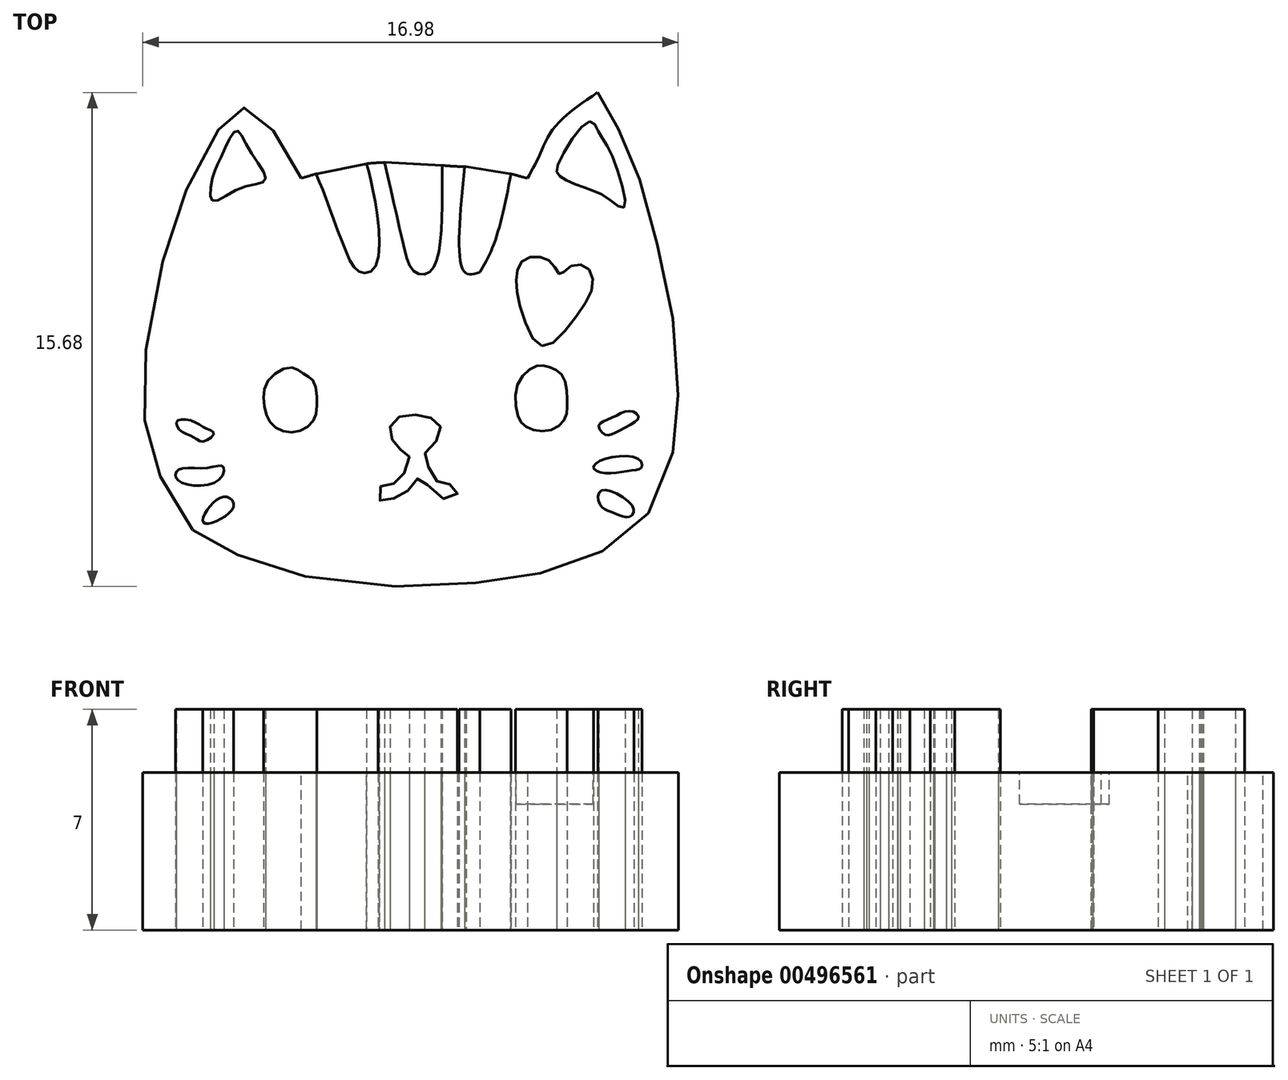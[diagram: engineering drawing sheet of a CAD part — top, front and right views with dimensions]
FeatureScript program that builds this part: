
annotation { "Feature Type Name" : "Feature", "Feature Type Description" : "" }
export const myFeature = defineFeature(function(context is Context, id is Id, definition is map)
    precondition{}
    {
        {
            var Q0;
            Q0=qCreatedBy(makeId("Top.planeOp"),FACE);
            var sketch = newSketch(context, id + "F0", { "sketchPlane" : qUnion([Q0])});
            skFitSpline(sketch, "E0", {"points": [v(16.94, 17.8) * mm, v(17.2, 17.42) * mm, v(17.74, 16.37) * mm, v(18.24, 15.15) * mm, v(18.74, 13.3) * mm, v(19.29, 10.91) * mm, v(19.5, 8.23) * mm, v(19.42, 6.84) * mm, v(18.87, 4.95) * mm, v(17.86, 3.74) * mm, v(16.35, 2.9) * mm, v(14.46, 2.4) * mm, v(12.5, 2.18) * mm, v(9.18, 2.18) * mm, v(6.15, 2.86) * mm, v(4.94, 3.4) * mm, v(3.93, 4.07) * mm, v(3.05, 5.67) * mm, v(2.63, 7.1) * mm, v(2.55, 8.94) * mm, v(3.13, 12.38) * mm, v(3.93, 14.77) * mm, v(4.9, 16.58) * mm, v(5.4, 17.46) * mm, v(5.86, 17.2) * mm, v(6.24, 16.96) * mm, v(6.87, 16.33) * mm, v(7.54, 15.07) * mm], "startDerivative": vector(11.95, -16.58) * mm, "endDerivative": vector(17.95, -39.41) * mm});
            skFitSpline(sketch, "E1", {"points": [v(7.54, 15.07) * mm, v(9, 15.44) * mm, v(10.77, 15.57) * mm, v(12.45, 15.44) * mm, v(13.29, 15.4) * mm, v(14.72, 15.07) * mm], "startDerivative": vector(6.98, 2.07) * mm, "endDerivative": vector(7.67, -2.1) * mm});
            skFitSpline(sketch, "E2", {"points": [v(14.72, 15.07) * mm, v(15.1, 15.78) * mm, v(15.55, 16.66) * mm, v(16.94, 17.8) * mm], "startDerivative": vector(1.42, 2.49) * mm, "endDerivative": vector(3.9, 2.68) * mm});
            skFitSpline(sketch, "E3", {"points": [v(15, 9.1) * mm, v(15.43, 9.07) * mm, v(15.85, 8.77) * mm, v(15.97, 8.02) * mm, v(15.93, 7.51) * mm, v(15.51, 7.1) * mm, v(14.76, 7.14) * mm, v(14.42, 7.51) * mm, v(14.42, 8.56) * mm, v(15, 9.1) * mm]});
            skFitSpline(sketch, "E4", {"points": [v(7.25, 9.07) * mm, v(7.62, 8.86) * mm, v(7.92, 8.65) * mm, v(8.04, 7.93) * mm, v(7.88, 7.3) * mm, v(7.25, 7) * mm, v(6.62, 7.26) * mm, v(6.36, 7.9) * mm, v(6.5, 8.65) * mm, v(7.25, 9.07) * mm]});
            skFitSpline(sketch, "E5", {"points": [v(4.73, 14.35) * mm, v(4.73, 15.07) * mm, v(5.02, 15.78) * mm, v(5.48, 16.58) * mm, v(5.86, 16.03) * mm, v(6.4, 15.02) * mm, v(5.65, 14.77) * mm, v(4.73, 14.35) * mm]});
            skFitSpline(sketch, "E6", {"points": [v(16.69, 16.87) * mm, v(16.98, 16.54) * mm, v(17.4, 15.78) * mm, v(17.78, 14.14) * mm, v(17.2, 14.48) * mm, v(16.4, 14.82) * mm, v(15.72, 15.15) * mm, v(15.68, 15.49) * mm, v(16.69, 16.87) * mm]});
            skFitSpline(sketch, "E7", {"points": [v(13.2, 12.09) * mm, v(13.67, 13.01) * mm, v(14.2, 15.2) * mm], "startDerivative": vector(1.2, 2) * mm, "endDerivative": vector(0.82, 4.1) * mm});
            skFitSpline(sketch, "E8", {"points": [v(14.2, 15.2) * mm, v(13.29, 15.4) * mm, v(12.45, 15.44) * mm], "startDerivative": vector(-1.79, 0.45) * mm, "endDerivative": vector(-1.7, 0.02) * mm});
            skFitSpline(sketch, "E9", {"points": [v(13.2, 12.09) * mm, v(12.73, 12.09) * mm, v(12.73, 15.44) * mm], "startDerivative": vector(-1.98, -0.63) * mm, "endDerivative": vector(0.63, 6.3) * mm});
            skFitSpline(sketch, "E10", {"points": [v(12.73, 15.44) * mm, v(14.2, 15.2) * mm], "startDerivative": vector(1.47, -0.23) * mm, "endDerivative": vector(1.47, -0.23) * mm});
            skFitSpline(sketch, "E11", {"points": [v(10.2, 15.57) * mm, v(10.77, 13.01) * mm, v(11.15, 12.09) * mm, v(11.6, 12.09) * mm, v(11.95, 13.01) * mm, v(12.01, 15.48) * mm], "startDerivative": vector(2.28, -10.08) * mm, "endDerivative": vector(-0.07, 9.99) * mm});
            skFitSpline(sketch, "E12", {"points": [v(12.01, 15.48) * mm, v(10.2, 15.57) * mm], "startDerivative": vector(-1.82, 0.1) * mm, "endDerivative": vector(-1.82, 0.1) * mm});
            skFitSpline(sketch, "E13", {"points": [v(8.02, 15.2) * mm, v(8.42, 14.19) * mm, v(9, 12.63) * mm, v(9.43, 12.09) * mm, v(9.89, 12.26) * mm, v(9.89, 14.31) * mm, v(9.62, 15.53) * mm], "startDerivative": vector(2.34, -5.71) * mm, "endDerivative": vector(-1.55, 5.88) * mm});
            skFitSpline(sketch, "E14", {"points": [v(9.62, 15.53) * mm, v(8.02, 15.2) * mm], "startDerivative": vector(-1.6, -0.32) * mm, "endDerivative": vector(-1.6, -0.32) * mm});
            skFitSpline(sketch, "E15", {"points": [v(10.06, 5.29) * mm, v(10.48, 5.37) * mm, v(10.85, 5.8) * mm, v(10.94, 6.34) * mm, v(10.6, 6.5) * mm, v(10.4, 6.88) * mm, v(10.4, 7.26) * mm, v(10.81, 7.56) * mm, v(11.44, 7.51) * mm, v(11.86, 7.35) * mm, v(11.95, 6.88) * mm, v(11.48, 6.38) * mm, v(11.57, 5.92) * mm, v(11.9, 5.41) * mm, v(12.32, 5.33) * mm, v(12.5, 5.04) * mm, v(11.9, 4.95) * mm, v(11.32, 5.58) * mm, v(11.02, 5.25) * mm, v(10.56, 4.95) * mm, v(10.06, 4.83) * mm, v(10.06, 5.29) * mm]});
            skFitSpline(sketch, "E16", {"points": [v(17.4, 7.47) * mm, v(17.99, 7.68) * mm, v(18.24, 7.47) * mm, v(17.61, 7.05) * mm, v(17.2, 6.93) * mm, v(16.98, 7.22) * mm, v(17.4, 7.47) * mm]});
            skFitSpline(sketch, "E17", {"points": [v(17.2, 6.17) * mm, v(18.28, 6.13) * mm, v(18.32, 5.88) * mm, v(17.99, 5.8) * mm, v(17.2, 5.7) * mm, v(16.81, 5.88) * mm, v(17.2, 6.17) * mm]});
            skFitSpline(sketch, "E18", {"points": [v(17.07, 5.16) * mm, v(18.07, 4.62) * mm, v(17.95, 4.32) * mm, v(17.44, 4.45) * mm, v(17.02, 4.7) * mm, v(17.07, 5.16) * mm]});
            skFitSpline(sketch, "E19", {"points": [v(4.43, 6.72) * mm, v(4.14, 6.84) * mm, v(3.72, 7.05) * mm, v(3.6, 7.35) * mm, v(4.01, 7.39) * mm, v(4.52, 7.14) * mm, v(4.77, 6.97) * mm, v(4.43, 6.72) * mm]});
            skFitSpline(sketch, "E20", {"points": [v(4.56, 5.88) * mm, v(3.68, 5.83) * mm, v(3.55, 5.62) * mm, v(3.85, 5.37) * mm, v(4.94, 5.5) * mm, v(5.06, 5.92) * mm, v(4.56, 5.88) * mm]});
            skFitSpline(sketch, "E21", {"points": [v(4.64, 4.66) * mm, v(5.19, 4.95) * mm, v(5.4, 4.66) * mm, v(4.77, 4.16) * mm, v(4.43, 4.16) * mm, v(4.64, 4.66) * mm]});
            skFitSpline(sketch, "E22", {"points": [v(15.18, 9.74) * mm, v(16.23, 10.64) * mm, v(16.8, 11.74) * mm, v(16.54, 12.28) * mm, v(16.02, 12.24) * mm, v(15.76, 12.02) * mm, v(15.54, 12.31) * mm, v(15.15, 12.56) * mm, v(14.59, 12.47) * mm, v(14.37, 11.96) * mm, v(14.5, 11) * mm, v(15.18, 9.74) * mm]});
            skSolve(sketch);
        }
        {
            var Q0;
            {var subQ0=sQuery(id+"F0.wireOp",EDGE,"E13");var subQ1=sQuery(id+"F0.wireOp",EDGE,"E1");var subQ2=makeQuery(id+"F0.imprint","INTERSECT",VERTEX,{"derivedFrom":[subQ1,subQ0]});Q0=makeQuery(id+"F0.imprint","IMPRINT",FACE,{"disambiguationData":[TD([[makeQuery(id+"F0.imprint","IMPRINT",EDGE,{"disambiguationData":[TD([[subQ2,-1.0]])],"derivedFrom":subQ1}),-1.0]])]});}
            var Q1;
            Q1=makeQuery(id+"F0.imprint","IMPRINT",FACE,{"disambiguationData":[TD([[makeQuery(id+"F0.imprint","IMPRINT",EDGE,{"derivedFrom":sQuery(id+"F0.wireOp",EDGE,"E11")}),1.0]])]});
            var Q2;
            {var subQ0=sQuery(id+"F0.wireOp",EDGE,"E9");var subQ3=sQuery(id+"F0.wireOp",EDGE,"E1");var subQ4=makeQuery(id+"F0.imprint","INTERSECT",VERTEX,{"derivedFrom":[subQ3,subQ0]});Q2=makeQuery(id+"F0.imprint","IMPRINT",FACE,{"disambiguationData":[TD([[makeQuery(id+"F0.imprint","IMPRINT",EDGE,{"disambiguationData":[TD([[subQ4,-1.0]])],"derivedFrom":subQ3}),-1.0]])]});}
            var Q3;
            Q3=makeQuery(id+"F0.imprint","IMPRINT",FACE,{"disambiguationData":[TD([[makeQuery(id+"F0.imprint","IMPRINT",EDGE,{"derivedFrom":sQuery(id+"F0.wireOp",EDGE,"E6")}),-1.0]])]});
            var Q4;
            Q4=makeQuery(id+"F0.imprint","IMPRINT",FACE,{"disambiguationData":[TD([[makeQuery(id+"F0.imprint","IMPRINT",EDGE,{"derivedFrom":sQuery(id+"F0.wireOp",EDGE,"E5")}),-1.0]])]});
            var Q5;
            Q5=makeQuery(id+"F0.imprint","IMPRINT",FACE,{"disambiguationData":[TD([[makeQuery(id+"F0.imprint","IMPRINT",EDGE,{"derivedFrom":sQuery(id+"F0.wireOp",EDGE,"E4")}),-1.0]])]});
            var Q6;
            Q6=makeQuery(id+"F0.imprint","IMPRINT",FACE,{"disambiguationData":[TD([[makeQuery(id+"F0.imprint","IMPRINT",EDGE,{"derivedFrom":sQuery(id+"F0.wireOp",EDGE,"E21")}),-1.0]])]});
            var Q7;
            Q7=makeQuery(id+"F0.imprint","IMPRINT",FACE,{"disambiguationData":[TD([[makeQuery(id+"F0.imprint","IMPRINT",EDGE,{"derivedFrom":sQuery(id+"F0.wireOp",EDGE,"E20")}),1.0]])]});
            var Q8;
            Q8=makeQuery(id+"F0.imprint","IMPRINT",FACE,{"disambiguationData":[TD([[makeQuery(id+"F0.imprint","IMPRINT",EDGE,{"derivedFrom":sQuery(id+"F0.wireOp",EDGE,"E19")}),-1.0]])]});
            var Q9;
            Q9=makeQuery(id+"F0.imprint","IMPRINT",FACE,{"disambiguationData":[TD([[makeQuery(id+"F0.imprint","IMPRINT",EDGE,{"derivedFrom":sQuery(id+"F0.wireOp",EDGE,"E15")}),-1.0]])]});
            var Q10;
            Q10=makeQuery(id+"F0.imprint","IMPRINT",FACE,{"disambiguationData":[TD([[makeQuery(id+"F0.imprint","IMPRINT",EDGE,{"derivedFrom":sQuery(id+"F0.wireOp",EDGE,"E3")}),-1.0]])]});
            var Q11;
            Q11=makeQuery(id+"F0.imprint","IMPRINT",FACE,{"disambiguationData":[TD([[makeQuery(id+"F0.imprint","IMPRINT",EDGE,{"derivedFrom":sQuery(id+"F0.wireOp",EDGE,"E16")}),-1.0]])]});
            var Q12;
            Q12=makeQuery(id+"F0.imprint","IMPRINT",FACE,{"disambiguationData":[TD([[makeQuery(id+"F0.imprint","IMPRINT",EDGE,{"derivedFrom":sQuery(id+"F0.wireOp",EDGE,"E17")}),-1.0]])]});
            var Q13;
            Q13=makeQuery(id+"F0.imprint","IMPRINT",FACE,{"disambiguationData":[TD([[makeQuery(id+"F0.imprint","IMPRINT",EDGE,{"derivedFrom":sQuery(id+"F0.wireOp",EDGE,"E18")}),-1.0]])]});
            extrude(context, id + "F1", {"entities" : qUnion([Q0, Q1, Q2, Q3, Q4, Q5, Q6, Q7, Q8, Q9, Q10, Q11, Q12, Q13]), "depth" : 7 * mm, "offsetDistance" : 25 * mm});
        }
        {
            var Q0;
            {var subQ5=sQuery(id+"F0.wireOp",EDGE,"E0");Q0=makeQuery(id+"F0.imprint","IMPRINT",FACE,{"disambiguationData":[TD([[makeQuery(id+"F0.imprint","IMPRINT",EDGE,{"derivedFrom":subQ5}),-1.0]])]});}
            extrude(context, id + "F2", {"entities" : qUnion([Q0]), "depth" : 5 * mm, "offsetDistance" : 25 * mm});
        }
        {
            var Q0;
            Q0=makeQuery(id+"F0.imprint","IMPRINT",FACE,{"disambiguationData":[TD([[makeQuery(id+"F0.imprint","IMPRINT",EDGE,{"derivedFrom":sQuery(id+"F0.wireOp",EDGE,"E22")}),1.0]])]});
            extrude(context, id + "F3", {"entities" : qUnion([Q0]), "operationType" : NewBodyOperationType.ADD, "depth" : 4 * mm, "offsetDistance" : 25 * mm});
        }
    });
